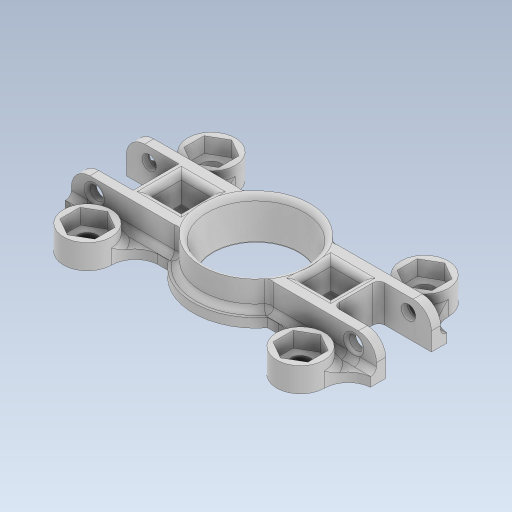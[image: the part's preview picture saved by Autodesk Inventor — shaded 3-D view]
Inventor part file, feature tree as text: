
AUTODESK INVENTOR PART (.ipt)
format: ipt  version: 2023 (Build 270158000, 158)  size: 1,230,848 bytes
history: native  units: in
note: dims shown in document units (in); Inventor stores cm internally (conversion verified against a paired STEP export)
features: sketch x9, extrude x8, fillet x6, projected_geometry x6, mirror x1, revolve x1
ambient origin geometry x8: Origin, YZ Plane, XZ Plane, XY Plane, X Axis, Y Axis, Z Axis, Center Point
bodies: Solid1 (feature_tree)
feature tree (31):
  extrude  "Extrusion1"  Depth=1.5748in
  extrude  "Extrusion2"  Depth=0.4134in
  fillet  "Fillet1"  Radius=1.517in
  extrude  "Extrusion3"  Depth=0.1181in
  fillet  "Fillet2"  Radius=0.4724in
  extrude  "Extrusion4"  Depth=0.3937in
  mirror  "Mirror1"
  fillet  "Fillet3"  Radius=0.5906in
  fillet  "Fillet4"  Radius=0.3937in
  revolve  "Revolution1"  [1 undecoded]
  fillet  "Fillet5"  Radius=0.185in
  extrude  "Extrusion5"  TaperAngle=0.0deg  [1 undecoded]
  extrude  "Extrusion7"  Depth=0.0394in
  extrude  "Extrusion8"  TaperAngle=90.0deg  [1 undecoded]
  extrude  "Extrusion9"  Depth=0.0748in
  fillet  "Fillet6"  Radius=0.3937in
  sketch  "Sketch1"  dims[d0=3.937in d1=1.5748in]
  sketch  "Sketch2"  dims[d2=0.0787in d3=0.0in d6=0.4134in d8=1.517in]
  sketch  "Sketch3"  dims[d9=0.1181in d10=0.1181in d11=0.4724in d12=0.0in]
  sketch  "Sketch4"  dims[d13=0.0787in d14=1.1024in d16=0.5906in d17=0.3937in d18=0.0in]
  sketch  "Sketch5"  dims[d19=0.0787in d20=0.2953in d21=0.185in]
  projected_geometry  "Projected Loop1"
  sketch  "Sketch7"  dims[d22=0.2953in d23=0.0in d24=0.0in]
  sketch  "Sketch9"  dims[d25=0.2362in d26=0.0394in]
  projected_geometry  "Projected Loop2"
  sketch  "Sketch10"  dims[d27=0.0591in d28=90.0deg]
  projected_geometry  "Projected Loop3"
  projected_geometry  "Projected Loop4"
  projected_geometry  "Projected Loop5"
  projected_geometry  "Projected Loop8"
  sketch  "Sketch15"  dims[d29=0.0787in d30=3.937in d31=0.3937in d32=0.0in d37=0.0787in d38=0.0in d42=0.1181in d43=0.0in d62=2.75in d63=1.6in d64=0.26in d65=0.6157in d67=0.7874in d69=2.75in d70=0.3937in d72=0.3937in d74=0.0748in d75=1.6in d76=2.75in d77=0.2598in d78=0.7874in d80=1.6in d81=0.7874in d83=2.75in d86=0.1969in d87=0.0in d39=0.0197in d40=0.0344in d41=0.0197in]
note: 3 required parameter values undecoded (feature->parameter linkage not recoverable at this tier; creation-order binding heuristic only, values carry confidence <= 0.55)